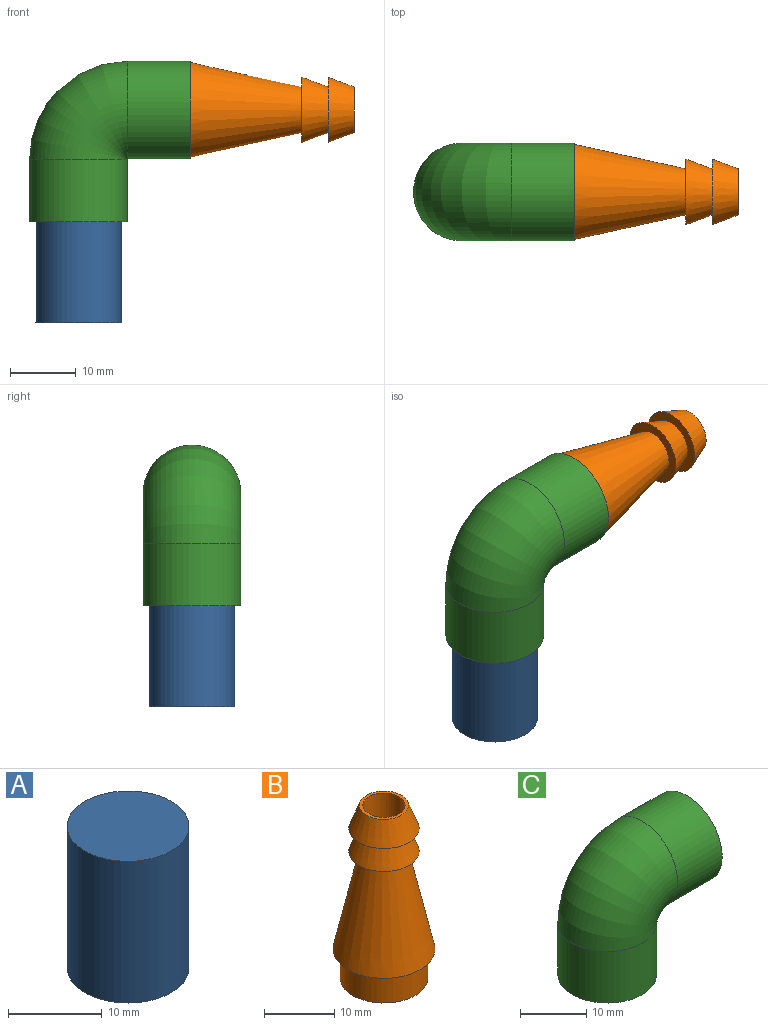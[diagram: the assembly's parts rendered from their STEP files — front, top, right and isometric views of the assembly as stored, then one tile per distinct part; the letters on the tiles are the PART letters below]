
ASSEMBLY  parts=3 mates=2
PART A: 3 faces, bbox 13x13x18.5 mm
  f0: cylinder r=6.5mm len=18.5mm, axis (0,0,-1), area 755.6mm2, adj f1,f2
  f1: plane 13x13mm, normal (0,0,1), area 132.7mm2, adj f0
  f2: plane 13x13mm, normal (0,0,-1), area 132.7mm2, adj f0
PART B: 12 faces, bbox 14.5x14.5x30 mm
  f0: plane 10x10mm, normal (0,0,-1), area 40.1mm2, adj f1,f11
  f1: cone r=3.5mm half-angle=20.6deg, axis (0,0,-1), area 114.1mm2, adj f0,f2
  f2: plane 7x7mm, normal (0,0,1), area 10.2mm2, adj f1,f3
  f3: cylinder r=3mm len=8mm, axis (0,0,-1), area 150.8mm2, adj f2,f4
  f4: cone r=3mm half-angle=9.2deg, axis (0,0,-1), area 473.4mm2, adj f3,f5
  f5: cylinder r=5.75mm len=11.5mm, axis (0,0,-1), area 180.6mm2, adj f4,f6
  f6: plane 12.5x12.5mm, normal (0,0,-1), area 18.8mm2, adj f5,f7
  f7: cylinder r=6.25mm len=12.5mm, axis (0,0,-1), area 196.3mm2, adj f6,f8
  f8: plane 14.5x14.5mm, normal (0,0,-1), area 42.4mm2, adj f7,f9
  f9: cone r=3.5mm half-angle=12.4deg, axis (0,0,-1), area 587.9mm2, adj f8,f10
  f10: plane 10x10mm, normal (0,0,-1), area 40.1mm2, adj f9,f11
  f11: cone r=3.5mm half-angle=20.6deg, axis (0,0,-1), area 114.1mm2, adj f0,f10
PART C: 8 faces, bbox 25.7x14.9x25.7 mm
  f0: plane 14.9x14.9mm, normal (0,0,-1), area 39.6mm2, adj f2,f5
  f1: plane 14.9x14.9mm, normal (1,0,0), area 39.6mm2, adj f4,f7
  f2: cylinder r=7.45mm len=14.9mm, axis (0,0,1), area 444.7mm2, adj f0,f3
  f3: torus R=7.55mm, axis (0,1,0), area 555.1mm2, adj f2,f4
  f4: cylinder r=7.45mm len=14.9mm, axis (1,0,0), area 444.7mm2, adj f1,f3
  f5: cylinder r=6.55mm len=13.1mm, axis (0,0,1), area 391mm2, adj f0,f6
  f6: torus R=7.55mm, axis (0,1,0), area 488.1mm2, adj f5,f7
  f7: cylinder r=6.55mm len=13.1mm, axis (1,0,0), area 391mm2, adj f1,f6
PLACE A t=(23.31,15.52,-12.29)mm
PLACE B rot(axis=(-0.58,0.58,-0.58),120deg) t=(35.36,15.52,20.14)mm
PLACE C t=(23.31,15.52,3.09)mm fixed
MATE slider B.f1 <-> C.f4  axis (-1,0,0) through (35.36,15.52,20.14)mm
MATE slider A.f0 <-> C.f5  axis (0,0,-1) through (23.31,15.52,6.21)mm
